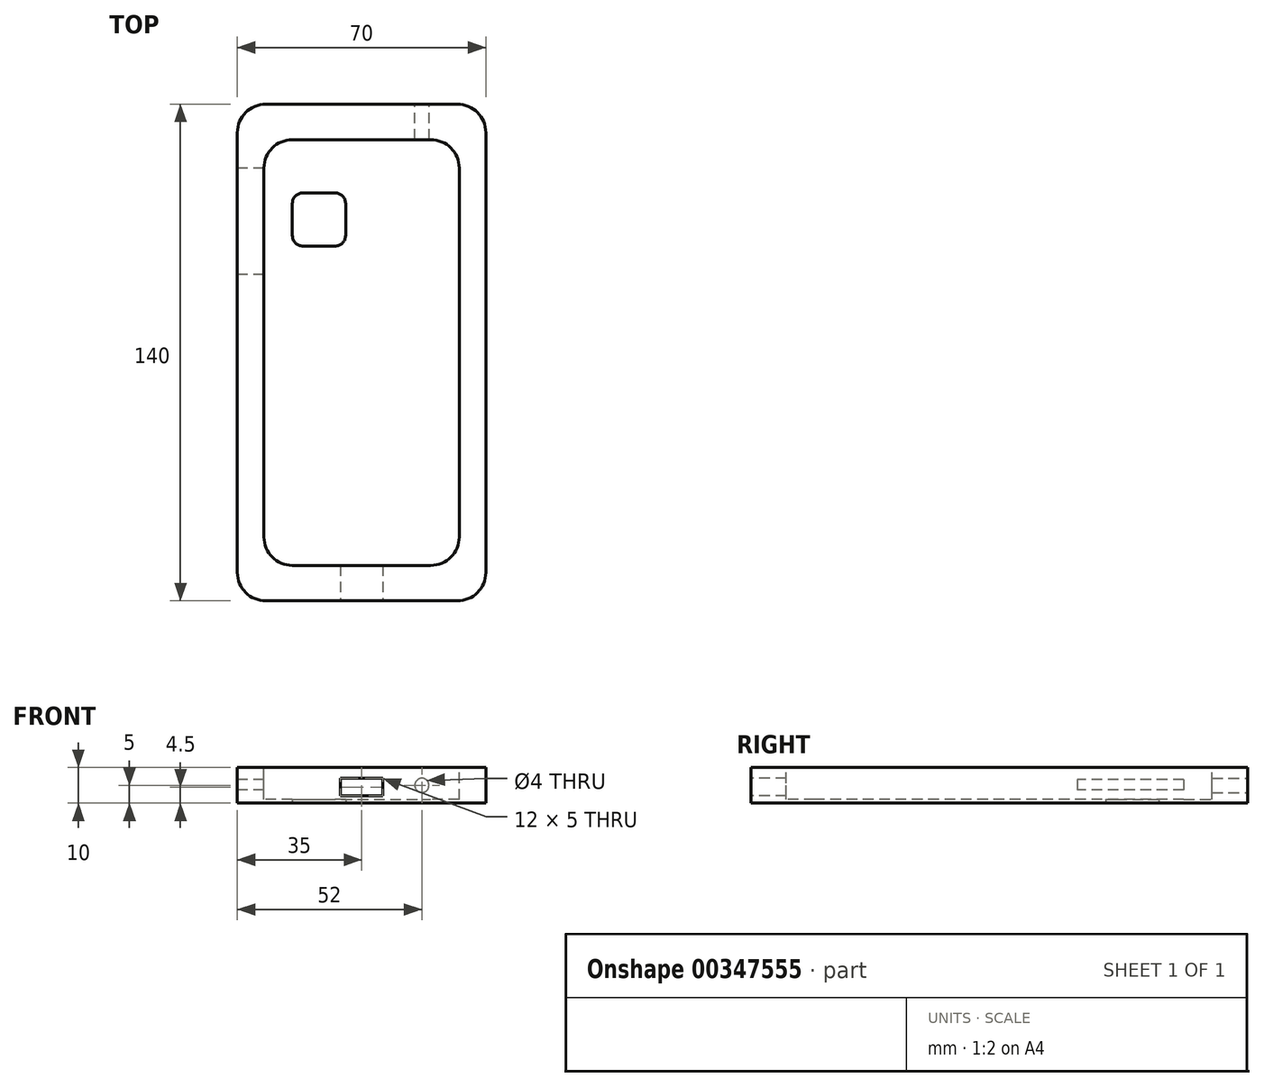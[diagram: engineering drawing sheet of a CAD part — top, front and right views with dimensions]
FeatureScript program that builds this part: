
annotation { "Feature Type Name" : "Feature", "Feature Type Description" : "" }
export const myFeature = defineFeature(function(context is Context, id is Id, definition is map)
    precondition{}
    {
        {
            var Q0;
            Q0=qCreatedBy(makeId("Top.planeOp"),FACE);
            var sketch = newSketch(context, id + "F0", { "sketchPlane" : qUnion([Q0])});
            skLineSegment(sketch, "E0.bottom", {"start": v(-35, 70) * mm, "end": v(35, 70) * mm});
            skLineSegment(sketch, "E0.top", {"start": v(-35, -70) * mm, "end": v(35, -70) * mm});
            skLineSegment(sketch, "E0.left", {"start": v(-35, 70) * mm, "end": v(-35, -70) * mm});
            skLineSegment(sketch, "E0.right", {"start": v(35, 70) * mm, "end": v(35, -70) * mm});
            skSolve(sketch);
        }
        {
            var Q0;
            Q0=makeQuery(id+"F0.imprint","IMPRINT",FACE,{"disambiguationData":[TD([[makeQuery(id+"F0.imprint","IMPRINT",EDGE,{"derivedFrom":sQuery(id+"F0.wireOp",EDGE,"E0.bottom")}),-1.0]])]});
            extrude(context, id + "F1", {"entities" : qUnion([Q0]), "depth" : 10 * mm});
        }
        {
            var Q0;
            Q0=makeQuery(id+"F1.opExtrude","CAP_FACE",FACE,{"disambiguationData":[OSD([sQuery(id+"F0.wireOp",EDGE,"E0.bottom"),sQuery(id+"F0.wireOp",EDGE,"E0.top"),sQuery(id+"F0.wireOp",EDGE,"E0.left"),sQuery(id+"F0.wireOp",EDGE,"E0.right")])],"isStart":false});
            var sketch = newSketch(context, id + "F2", { "sketchPlane" : qUnion([Q0])});
            skLineSegment(sketch, "E1.bottom", {"start": v(-19.5, 60) * mm, "end": v(19.5, 60) * mm});
            skLineSegment(sketch, "E1.top", {"start": v(-19.5, -60) * mm, "end": v(19.5, -60) * mm});
            skLineSegment(sketch, "E1.left", {"start": v(-27.5, 52) * mm, "end": v(-27.5, -52) * mm});
            skLineSegment(sketch, "E1.right", {"start": v(27.5, 52) * mm, "end": v(27.5, -52) * mm});
            skPoint(sketch, "E2.visualSharp", {"position": v(-27.5, 60) * mm});
            skArc(sketch, "E2.filletArc", {"start": v(-19.5, 60) * mm, "mid": v(-25.16, 57.66) * mm, "end": v(-27.5, 52) * mm});
            skPoint(sketch, "E3.visualSharp", {"position": v(27.5, 60) * mm});
            skArc(sketch, "E3.filletArc", {"start": v(27.5, 52) * mm, "mid": v(25.16, 57.66) * mm, "end": v(19.5, 60) * mm});
            skPoint(sketch, "E4.visualSharp", {"position": v(27.5, -60) * mm});
            skArc(sketch, "E4.filletArc", {"start": v(19.5, -60) * mm, "mid": v(25.16, -57.66) * mm, "end": v(27.5, -52) * mm});
            skPoint(sketch, "E5.visualSharp", {"position": v(-27.5, -60) * mm});
            skArc(sketch, "E5.filletArc", {"start": v(-27.5, -52) * mm, "mid": v(-25.16, -57.66) * mm, "end": v(-19.5, -60) * mm});
            skSolve(sketch);
        }
        {
            var Q0;
            Q0=makeQuery(id+"F1.opExtrude","SWEPT_EDGE",EDGE,{"disambiguationData":[OSD([sQuery(id+"F0.wireOp",EDGE,"E0.bottom"),sQuery(id+"F0.wireOp",EDGE,"E0.right")])]});
            var Q1;
            Q1=makeQuery(id+"F1.opExtrude","SWEPT_EDGE",EDGE,{"disambiguationData":[OSD([sQuery(id+"F0.wireOp",EDGE,"E0.bottom"),sQuery(id+"F0.wireOp",EDGE,"E0.left")])]});
            var Q2;
            Q2=makeQuery(id+"F1.opExtrude","SWEPT_EDGE",EDGE,{"disambiguationData":[OSD([sQuery(id+"F0.wireOp",EDGE,"E0.top"),sQuery(id+"F0.wireOp",EDGE,"E0.right")])]});
            var Q3;
            Q3=makeQuery(id+"F1.opExtrude","SWEPT_EDGE",EDGE,{"disambiguationData":[OSD([sQuery(id+"F0.wireOp",EDGE,"E0.top"),sQuery(id+"F0.wireOp",EDGE,"E0.left")])]});
            fillet(context, id + "F3", {"entities" : qUnion([Q0, Q1, Q2, Q3]), "radius" : 8 * mm, "tangentPropagation" : true, "allowEdgeOverflow" : false});
        }
        {
            var Q0;
            Q0 = qSketchRegion(id + "F2", true);
            extrude(context, id + "F4", {"entities" : qUnion([Q0]), "operationType" : NewBodyOperationType.REMOVE, "oppositeDirection" : true, "depth" : 9 * mm});
        }
        {
            var Q0;
            Q0=makeQuery(id+"F4.boolean.opBoolean","COPY",FACE,{"derivedFrom":makeQuery(id+"F4.opExtrude","CAP_FACE",FACE,{"disambiguationData":[OSD([sQuery(id+"F2.wireOp",EDGE,"E1.bottom"),sQuery(id+"F2.wireOp",EDGE,"E1.top"),sQuery(id+"F2.wireOp",EDGE,"E1.left"),sQuery(id+"F2.wireOp",EDGE,"E1.right"),sQuery(id+"F2.wireOp",EDGE,"E2.filletArc"),sQuery(id+"F2.wireOp",EDGE,"E3.filletArc"),sQuery(id+"F2.wireOp",EDGE,"E4.filletArc"),sQuery(id+"F2.wireOp",EDGE,"E5.filletArc")])],"isStart":false})});
            var sketch = newSketch(context, id + "F5", { "sketchPlane" : qUnion([Q0])});
            skLineSegment(sketch, "E6.bottom", {"start": v(-16.5, 45) * mm, "end": v(-7.5, 45) * mm});
            skLineSegment(sketch, "E6.top", {"start": v(-16.5, 30) * mm, "end": v(-7.5, 30) * mm});
            skLineSegment(sketch, "E6.left", {"start": v(-19.5, 42) * mm, "end": v(-19.5, 33) * mm});
            skLineSegment(sketch, "E6.right", {"start": v(-4.5, 42) * mm, "end": v(-4.5, 33) * mm});
            skPoint(sketch, "E7.visualSharp", {"position": v(-19.5, 45) * mm});
            skArc(sketch, "E7.filletArc", {"start": v(-16.5, 45) * mm, "mid": v(-18.62, 44.12) * mm, "end": v(-19.5, 42) * mm});
            skPoint(sketch, "E8.visualSharp", {"position": v(-4.5, 45) * mm});
            skArc(sketch, "E8.filletArc", {"start": v(-4.5, 42) * mm, "mid": v(-5.38, 44.12) * mm, "end": v(-7.5, 45) * mm});
            skPoint(sketch, "E9.visualSharp", {"position": v(-4.5, 30) * mm});
            skArc(sketch, "E9.filletArc", {"start": v(-7.5, 30) * mm, "mid": v(-5.38, 30.88) * mm, "end": v(-4.5, 33) * mm});
            skPoint(sketch, "E10.visualSharp", {"position": v(-19.5, 30) * mm});
            skArc(sketch, "E10.filletArc", {"start": v(-19.5, 33) * mm, "mid": v(-18.62, 30.88) * mm, "end": v(-16.5, 30) * mm});
            skSolve(sketch);
        }
        {
            var Q0;
            Q0=makeQuery(id+"F5.imprint","IMPRINT",FACE,{"disambiguationData":[TD([[makeQuery(id+"F5.imprint","IMPRINT",EDGE,{"derivedFrom":sQuery(id+"F5.wireOp",EDGE,"E6.bottom")}),-1.0]])]});
            extrude(context, id + "F6", {"entities" : qUnion([Q0]), "operationType" : NewBodyOperationType.REMOVE, "endBound" : BoundingType.THROUGH_ALL, "oppositeDirection" : true, "depth" : 50 * mm, "hasDraft" : true, "draftAngle" : 3 * degree});
        }
        {
            var Q0;
            Q0=makeQuery(id+"F1.opExtrude","SWEPT_FACE",FACE,{"disambiguationData":[OSD([sQuery(id+"F0.wireOp",EDGE,"E0.top")])]});
            var sketch = newSketch(context, id + "F7", { "sketchPlane" : qUnion([Q0])});
            skLineSegment(sketch, "E11.bottom", {"start": v(-6, 7) * mm, "end": v(6, 7) * mm});
            skLineSegment(sketch, "E11.top", {"start": v(-6, 2) * mm, "end": v(6, 2) * mm});
            skLineSegment(sketch, "E11.left", {"start": v(-6, 7) * mm, "end": v(-6, 2) * mm});
            skLineSegment(sketch, "E11.right", {"start": v(6, 7) * mm, "end": v(6, 2) * mm});
            skSolve(sketch);
        }
        {
            var Q0;
            Q0=makeQuery(id+"F1.opExtrude","SWEPT_FACE",FACE,{"disambiguationData":[OSD([sQuery(id+"F0.wireOp",EDGE,"E0.left")])]});
            var sketch = newSketch(context, id + "F8", { "sketchPlane" : qUnion([Q0])});
            skLineSegment(sketch, "E12.bottom", {"start": v(-52, 6.68) * mm, "end": v(-22, 6.68) * mm});
            skLineSegment(sketch, "E12.top", {"start": v(-52, 3.68) * mm, "end": v(-22, 3.68) * mm});
            skLineSegment(sketch, "E12.left", {"start": v(-52, 6.68) * mm, "end": v(-52, 3.68) * mm});
            skLineSegment(sketch, "E12.right", {"start": v(-22, 6.68) * mm, "end": v(-22, 3.68) * mm});
            skSolve(sketch);
        }
        {
            var Q0;
            Q0 = qSketchRegion(id + "F8", true);
            extrude(context, id + "F9", {"entities" : qUnion([Q0]), "operationType" : NewBodyOperationType.REMOVE, "endBound" : BoundingType.UP_TO_NEXT, "oppositeDirection" : true, "depth" : 6.8 * mm});
        }
        {
            var Q0;
            Q0=makeQuery(id+"F1.opExtrude","SWEPT_FACE",FACE,{"disambiguationData":[OSD([sQuery(id+"F0.wireOp",EDGE,"E0.bottom")])]});
            var sketch = newSketch(context, id + "F10", { "sketchPlane" : qUnion([Q0])});
            skCircle(sketch, "E13", {"center": v(-17, 5) * mm, "radius": 2 * mm});
            skSolve(sketch);
        }
        {
            var Q0;
            Q0 = qSketchRegion(id + "F10", true);
            extrude(context, id + "F11", {"entities" : qUnion([Q0]), "operationType" : NewBodyOperationType.REMOVE, "oppositeDirection" : true, "depth" : 25 * mm});
        }
        {
            var Q0;
            Q0 = qSketchRegion(id + "F7", true);
            extrude(context, id + "F12", {"entities" : qUnion([Q0]), "operationType" : NewBodyOperationType.REMOVE, "endBound" : BoundingType.UP_TO_NEXT, "oppositeDirection" : true, "depth" : 25 * mm});
        }
    });
